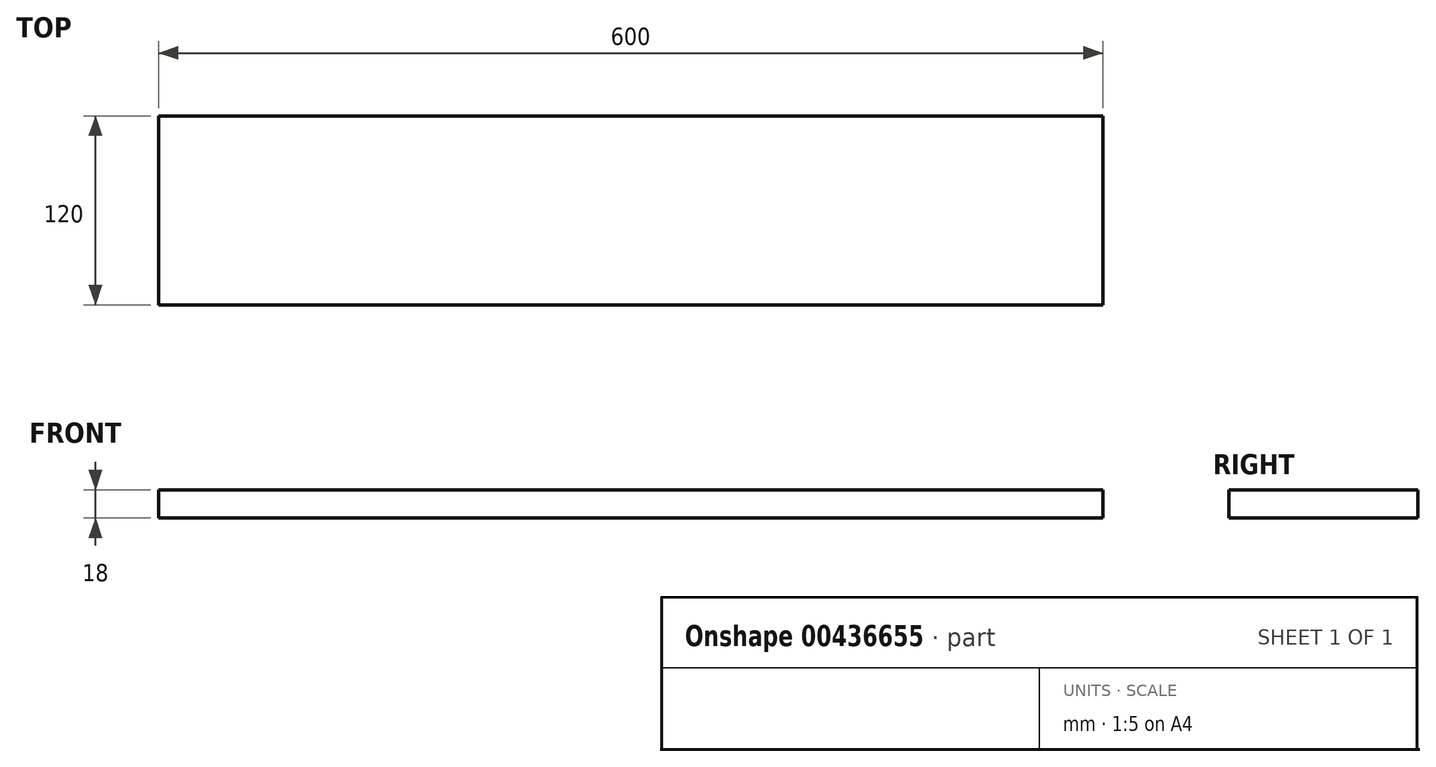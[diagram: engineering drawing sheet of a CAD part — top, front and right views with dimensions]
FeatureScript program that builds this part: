
annotation { "Feature Type Name" : "Feature", "Feature Type Description" : "" }
export const myFeature = defineFeature(function(context is Context, id is Id, definition is map)
    precondition{}
    {
        {
            var Q0;
            Q0=qCreatedBy(makeId("Right.planeOp"),FACE);
            var sketch = newSketch(context, id + "F0", { "sketchPlane" : qUnion([Q0])});
            skLineSegment(sketch, "E0.bottom", {"start": v(60, 9) * mm, "end": v(-60, 9) * mm});
            skLineSegment(sketch, "E0.top", {"start": v(60, -9) * mm, "end": v(-60, -9) * mm});
            skLineSegment(sketch, "E0.left", {"start": v(60, 9) * mm, "end": v(60, -9) * mm});
            skLineSegment(sketch, "E0.right", {"start": v(-60, 9) * mm, "end": v(-60, -9) * mm});
            skPoint(sketch, "E0.middle", {"position": v(0, 0) * mm});
            skSolve(sketch);
        }
        {
            var Q0;
            Q0=qSketchRegion(id+"F0",true);
            extrude(context, id + "F1", {"entities" : qUnion([Q0]), "depth" : 600 * mm});
        }
    });
